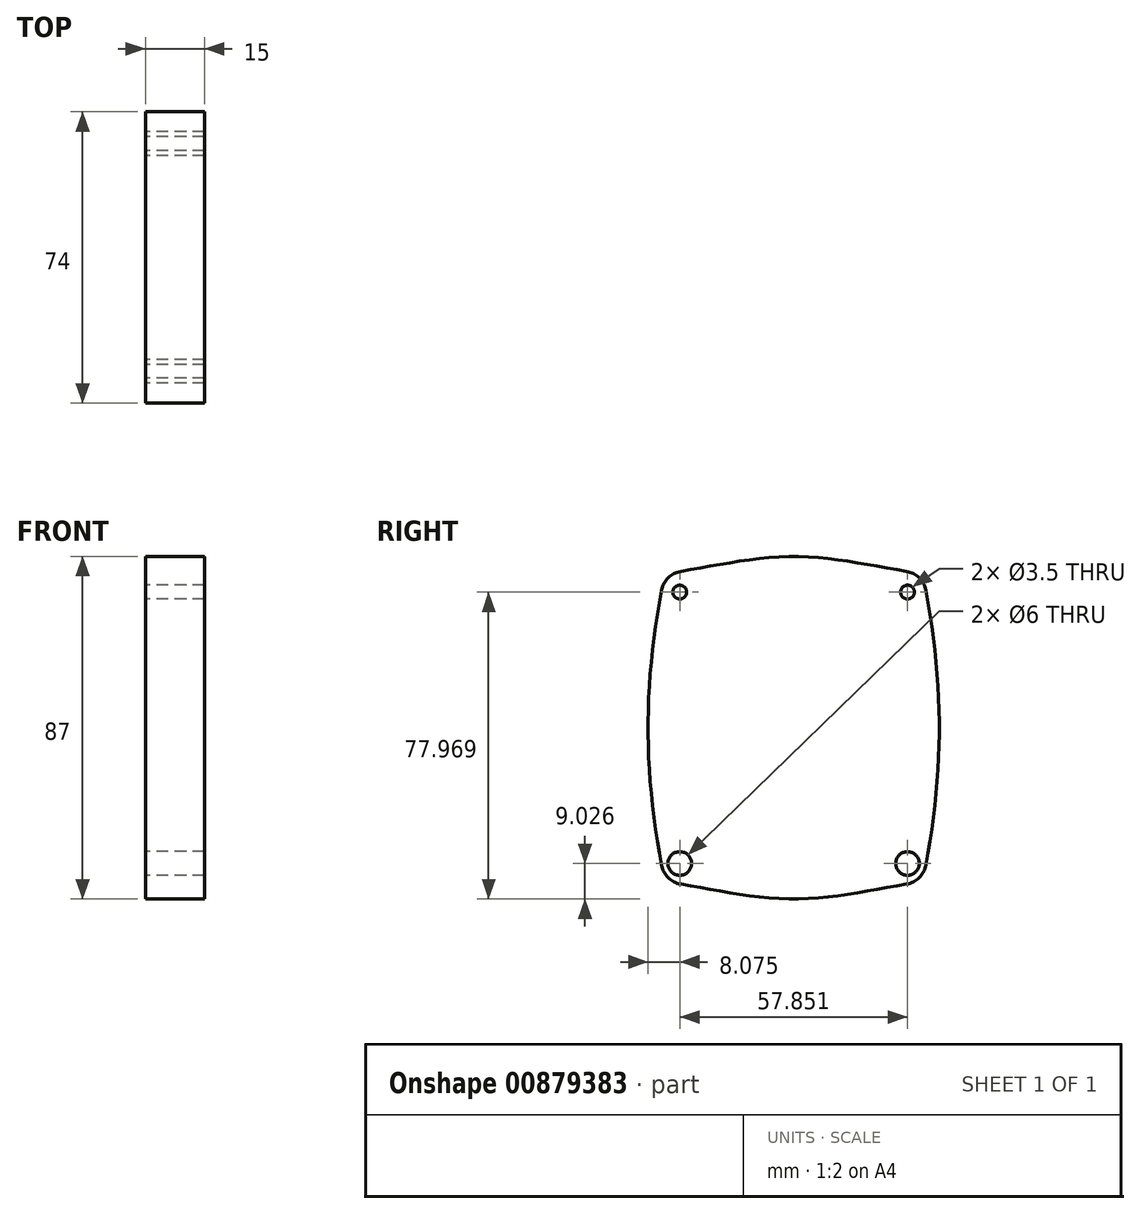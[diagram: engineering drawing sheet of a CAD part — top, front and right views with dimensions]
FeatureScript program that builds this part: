
annotation { "Feature Type Name" : "Feature", "Feature Type Description" : "" }
export const myFeature = defineFeature(function(context is Context, id is Id, definition is map)
    precondition{}
    {
        {
            var Q0;
            Q0=qCreatedBy(makeId("Right.planeOp"),FACE);
            var sketch = newSketch(context, id + "F0", { "sketchPlane" : qUnion([Q0])});
            skPoint(sketch, "E0", {"position": v(0.08, 102.9) * mm});
            skPoint(sketch, "E1", {"position": v(0.08, 15.9) * mm});
            skPoint(sketch, "E2", {"position": v(-36.92, 59.4) * mm});
            skPoint(sketch, "E3", {"position": v(37.08, 59.4) * mm});
            skPoint(sketch, "E4", {"position": v(29, 93.88) * mm});
            skCircle(sketch, "E5", {"center": v(29, 93.88) * mm, "radius": 3 * mm});
            skCircle(sketch, "E6", {"center": v(-28.85, 93.88) * mm, "radius": 3 * mm});
            skLineSegment(sketch, "E7", {"start": v(0.08, 59.4) * mm, "end": v(0, 59.4) * mm});
            skLineSegment(sketch, "E8", {"start": v(0, 59.4) * mm, "end": v(0.08, 59.4) * mm});
            skPoint(sketch, "E9.MirrorP", {"position": v(29, 24.94) * mm});
            skCircle(sketch, "E10.MirrorC", {"center": v(-28.85, 24.94) * mm, "radius": 3 * mm});
            skCircle(sketch, "E11.MirrorC", {"center": v(29, 24.94) * mm, "radius": 3 * mm});
            skPoint(sketch, "E12", {"position": v(32.86, 98.48) * mm});
            skPoint(sketch, "E13.MirrorP", {"position": v(-32.7, 98.48) * mm});
            skPoint(sketch, "E14.MirrorP", {"position": v(32.86, 20.34) * mm});
            skPoint(sketch, "E15.MirrorP", {"position": v(-32.7, 20.34) * mm});
            skFitSpline(sketch, "E16", {"points": [v(32.86, 98.48) * mm, v(0.08, 102.9) * mm, v(-32.7, 98.48) * mm], "startDerivative": vector(-65.56, 9.7) * mm, "endDerivative": vector(-65.56, -9.7) * mm});
            skFitSpline(sketch, "E17", {"points": [v(-32.7, 98.48) * mm, v(-36.92, 59.4) * mm, v(-32.7, 20.34) * mm], "startDerivative": vector(-15.65, -78.14) * mm, "endDerivative": vector(15.65, -78.14) * mm});
            skFitSpline(sketch, "E18", {"points": [v(-32.7, 20.34) * mm, v(0.08, 15.9) * mm, v(32.86, 20.34) * mm], "startDerivative": vector(65.56, -9.7) * mm, "endDerivative": vector(65.56, 9.7) * mm});
            skFitSpline(sketch, "E19", {"points": [v(32.86, 20.34) * mm, v(37.08, 59.4) * mm, v(32.86, 98.48) * mm], "startDerivative": vector(15.65, 78.14) * mm, "endDerivative": vector(-15.65, 78.14) * mm});
            skCircle(sketch, "E20", {"center": v(29, 93.88) * mm, "radius": 1.75 * mm});
            skCircle(sketch, "E21", {"center": v(-28.85, 93.88) * mm, "radius": 1.75 * mm});
            skCircle(sketch, "E22", {"center": v(29, 24.94) * mm, "radius": 1.75 * mm});
            skCircle(sketch, "E23", {"center": v(-28.85, 24.94) * mm, "radius": 1.75 * mm});
            skPoint(sketch, "E24.orphan", {"position": v(0.08, 59.4) * mm});
            skArc(sketch, "E25.filletArc", {"start": v(33.66, 94.3) * mm, "mid": v(31.98, 97.49) * mm, "end": v(28.77, 99.13) * mm});
            skArc(sketch, "E26.filletArc", {"start": v(-28.6, 99.13) * mm, "mid": v(-31.82, 97.49) * mm, "end": v(-33.5, 94.3) * mm});
            skArc(sketch, "E27.filletArc", {"start": v(-33.5, 24.52) * mm, "mid": v(-31.82, 21.33) * mm, "end": v(-28.6, 19.69) * mm});
            skArc(sketch, "E28.filletArc", {"start": v(28.77, 19.69) * mm, "mid": v(31.98, 21.33) * mm, "end": v(33.66, 24.52) * mm});
            skSolve(sketch);
        }
        {
            var Q0;
            Q0=makeQuery(id+"F0.imprint","IMPRINT",FACE,{"disambiguationData":[TD([[makeQuery(id+"F0.imprint","IMPRINT",EDGE,{"derivedFrom":sQuery(id+"F0.wireOp",EDGE,"E5")}),-1.0]])]});
            var Q1;
            Q1=makeQuery(id+"F0.imprint","IMPRINT",FACE,{"disambiguationData":[TD([[makeQuery(id+"F0.imprint","IMPRINT",EDGE,{"derivedFrom":sQuery(id+"F0.wireOp",EDGE,"E5")}),1.0]])]});
            var Q2;
            Q2=makeQuery(id+"F0.imprint","IMPRINT",FACE,{"disambiguationData":[TD([[makeQuery(id+"F0.imprint","IMPRINT",EDGE,{"derivedFrom":sQuery(id+"F0.wireOp",EDGE,"E6")}),1.0]])]});
            var Q3;
            Q3=makeQuery(id+"F0.imprint","IMPRINT",FACE,{"disambiguationData":[TD([[makeQuery(id+"F0.imprint","IMPRINT",EDGE,{"derivedFrom":sQuery(id+"F0.wireOp",EDGE,"E10.MirrorC")}),-1.0]])]});
            var Q4;
            Q4=makeQuery(id+"F0.imprint","IMPRINT",FACE,{"disambiguationData":[TD([[makeQuery(id+"F0.imprint","IMPRINT",EDGE,{"derivedFrom":sQuery(id+"F0.wireOp",EDGE,"E11.MirrorC")}),-1.0]])]});
            extrude(context, id + "F1", {"entities" : qUnion([Q0, Q1, Q2, Q3, Q4]), "depth" : 15 * mm, "offsetDistance" : 25 * mm});
        }
    });
